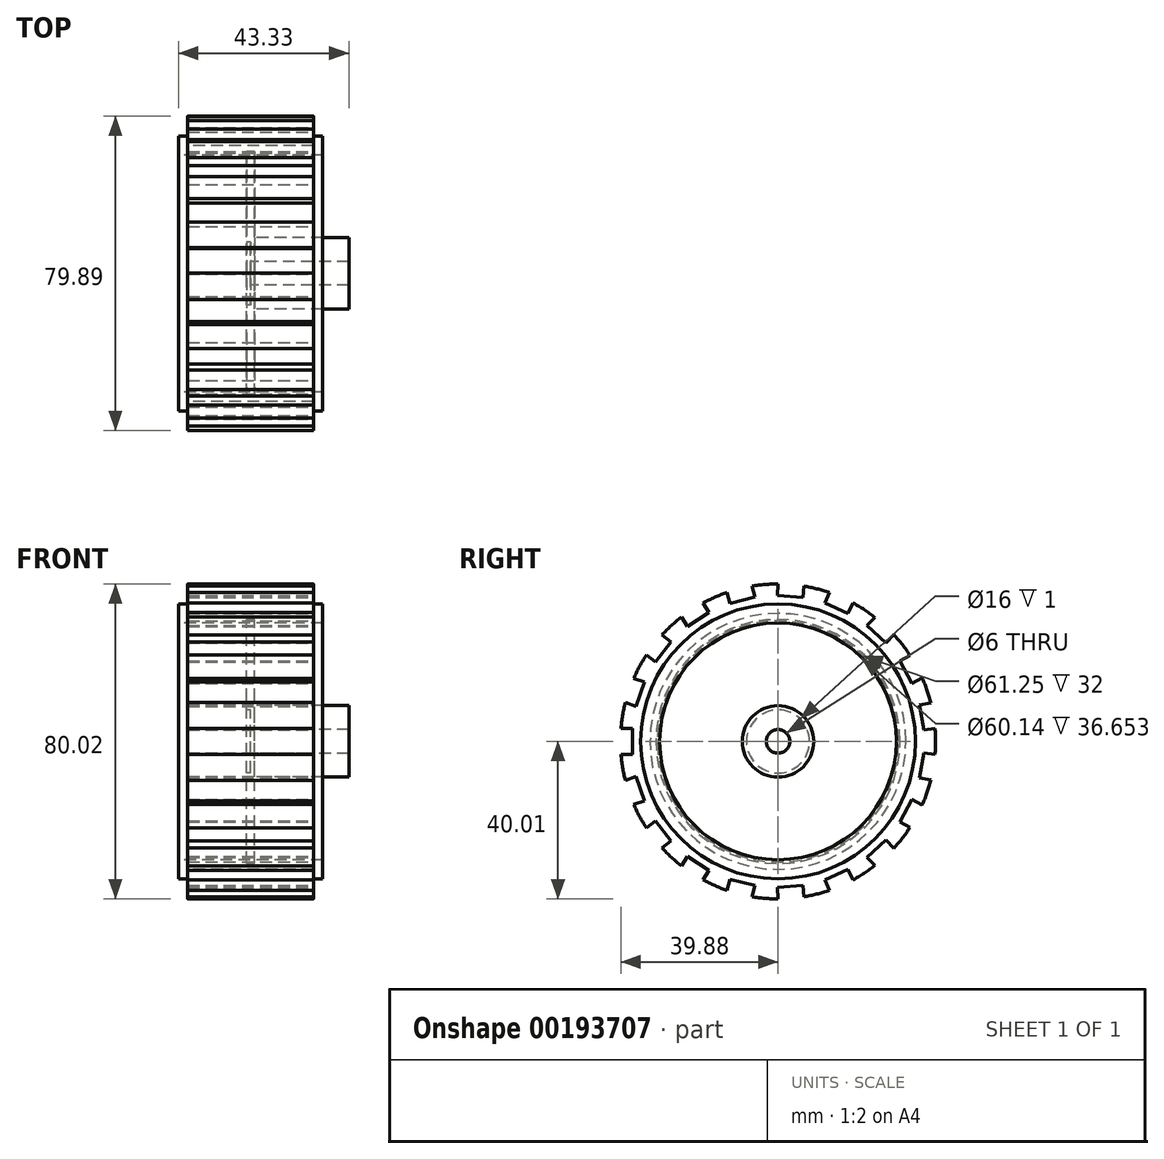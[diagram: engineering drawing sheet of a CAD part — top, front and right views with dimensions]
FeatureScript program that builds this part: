
annotation { "Feature Type Name" : "Feature", "Feature Type Description" : "" }
export const myFeature = defineFeature(function(context is Context, id is Id, definition is map)
    precondition{}
    {
        {
            var Q0;
            Q0=qCreatedBy(makeId("Front.planeOp"),FACE);
            var sketch = newSketch(context, id + "F0", { "sketchPlane" : qUnion([Q0])});
            skLineSegment(sketch, "E0.0", {"start": v(0, 32.5) * mm, "end": v(16, 32.5) * mm});
            skLineSegment(sketch, "E1", {"start": v(16, 32.5) * mm, "end": v(16, 34.92) * mm});
            skLineSegment(sketch, "E2", {"start": v(16, 34.92) * mm, "end": v(18.33, 34.92) * mm});
            skLineSegment(sketch, "E3", {"start": v(18.33, 34.92) * mm, "end": v(18.33, 30.07) * mm});
            skLineSegment(sketch, "E4", {"start": v(18.33, 30.07) * mm, "end": v(0, 30.07) * mm});
            skLineSegment(sketch, "E5.MirrorCS", {"start": v(-16, 32.5) * mm, "end": v(-16, 34.92) * mm});
            skLineSegment(sketch, "E6.MirrorCS", {"start": v(-16, 34.92) * mm, "end": v(-18.33, 34.92) * mm});
            skLineSegment(sketch, "E7.MirrorCS", {"start": v(0, 32.5) * mm, "end": v(-16, 32.5) * mm});
            skLineSegment(sketch, "E8.MirrorCS", {"start": v(-18.33, 34.92) * mm, "end": v(-18.33, 30.07) * mm});
            skLineSegment(sketch, "E9.MirrorCS", {"start": v(-18.33, 30.07) * mm, "end": v(0, 30.07) * mm});
            skLineSegment(sketch, "E10", {"start": v(-8.59, 0) * mm, "end": v(10.8, 0) * mm});
            skSolve(sketch);
        }
        {
            var Q0;
            Q0=makeQuery(id+"F0.imprint","IMPRINT",FACE,{"disambiguationData":[TD([[makeQuery(id+"F0.imprint","IMPRINT",EDGE,{"derivedFrom":sQuery(id+"F0.wireOp",EDGE,"E0.0")}),-1.0]])]});
            var Q1;
            Q1=sQuery(id+"F0.wireOp",EDGE,"E10");
            revolve(context, id + "F1", {"entities" : qUnion([Q0]), "axis" : qUnion([Q1]), "revolveType" : RevolveType.FULL});
        }
        {
            var Q0;
            Q0=qCreatedBy(makeId("Right.planeOp"),FACE);
            var sketch = newSketch(context, id + "F2", { "sketchPlane" : qUnion([Q0])});
            skCircle(sketch, "E11", {"center": v(0, 0) * mm, "radius": 31 * mm});
            skCircle(sketch, "E12", {"center": v(0, 0) * mm, "radius": 8 * mm});
            skCircle(sketch, "E13", {"center": v(0, 0) * mm, "radius": 3 * mm});
            skSolve(sketch);
        }
        {
            var Q0;
            Q0=makeQuery(id+"F2.imprint","IMPRINT",FACE,{"disambiguationData":[TD([[makeQuery(id+"F2.imprint","IMPRINT",EDGE,{"derivedFrom":sQuery(id+"F2.wireOp",EDGE,"E11")}),1.0]])]});
            extrude(context, id + "F3", {"entities" : qUnion([Q0]), "depth" : 1 * mm, "hasSecondDirection" : true, "secondDirectionOppositeDirection" : true, "secondDirectionDepth" : 1 * mm});
        }
        {
            var Q0;
            Q0=qCreatedBy(makeId("Right.planeOp"),FACE);
            var sketch = newSketch(context, id + "F4", { "sketchPlane" : qUnion([Q0])});
            skCircle(sketch, "E14", {"center": v(0, 0) * mm, "radius": 9.08 * mm});
            skCircle(sketch, "E15", {"center": v(0, 0) * mm, "radius": 3 * mm});
            skSolve(sketch);
        }
        {
            var Q0;
            Q0=qSketchRegion(id+"F4",true);
            extrude(context, id + "F5", {"entities" : qUnion([Q0]), "operationType" : NewBodyOperationType.ADD, "depth" : 25 * mm});
        }
        {
            var Q0;
            Q0=qCreatedBy(makeId("Right.planeOp"),FACE);
            cPlane(context, id + "F6", {"entities" : qUnion([Q0]), "cplaneType" : CPlaneType.OFFSET, "offset" : 16 * mm, "width" : 150 * mm, "height" : 150 * mm});
        }
        {
            var Q0;
            Q0=qCreatedBy(id+"F6.planeOp",FACE);
            var sketch = newSketch(context, id + "F7", { "sketchPlane" : qUnion([Q0])});
            skCircle(sketch, "E16", {"center": v(0, 0) * mm, "radius": 30.63 * mm});
            skCircle(sketch, "E17", {"center": v(0, 0) * mm, "radius": 40.01 * mm});
            skSolve(sketch);
        }
        {
            var Q0;
            Q0=qSketchRegion(id+"F7",true);
            extrude(context, id + "F8", {"entities" : qUnion([Q0]), "oppositeDirection" : true, "depth" : 32 * mm});
        }
        {
            var Q0;
            Q0=qCreatedBy(id+"F6.planeOp",FACE);
            var sketch = newSketch(context, id + "F9", { "sketchPlane" : qUnion([Q0])});
            skLineSegment(sketch, "E18.bottom", {"start": v(-36.97, -3.26) * mm, "end": v(-46.27, -3.26) * mm});
            skLineSegment(sketch, "E18.top", {"start": v(-36.97, 3.26) * mm, "end": v(-46.27, 3.26) * mm});
            skLineSegment(sketch, "E18.left", {"start": v(-36.97, -3.26) * mm, "end": v(-36.97, 3.26) * mm});
            skLineSegment(sketch, "E18.right", {"start": v(-46.27, -3.26) * mm, "end": v(-46.27, 3.26) * mm});
            skPoint(sketch, "E18.middle", {"position": v(-41.62, 0) * mm});
            skPoint(sketch, "E19.1.0", {"position": v(-39.37, 13.52) * mm});
            skLineSegment(sketch, "E19.1.1", {"start": v(-36.03, 8.93) * mm, "end": v(-44.82, 11.95) * mm});
            skLineSegment(sketch, "E19.1.2", {"start": v(-33.91, 15.08) * mm, "end": v(-42.71, 18.1) * mm});
            skLineSegment(sketch, "E19.1.3", {"start": v(-36.03, 8.93) * mm, "end": v(-33.91, 15.08) * mm});
            skLineSegment(sketch, "E19.1.4", {"start": v(-44.82, 11.95) * mm, "end": v(-42.71, 18.1) * mm});
            skPoint(sketch, "E19.2.0", {"position": v(-32.85, 25.57) * mm});
            skLineSegment(sketch, "E19.2.1", {"start": v(-31.18, 20.14) * mm, "end": v(-38.52, 25.85) * mm});
            skLineSegment(sketch, "E19.2.2", {"start": v(-27.18, 25.28) * mm, "end": v(-34.52, 31) * mm});
            skLineSegment(sketch, "E19.2.3", {"start": v(-31.18, 20.14) * mm, "end": v(-27.18, 25.28) * mm});
            skLineSegment(sketch, "E19.2.4", {"start": v(-38.52, 25.85) * mm, "end": v(-34.52, 31) * mm});
            skPoint(sketch, "E19.3.0", {"position": v(-22.77, 34.85) * mm});
            skLineSegment(sketch, "E19.3.1", {"start": v(-22.95, 29.17) * mm, "end": v(-28.04, 36.96) * mm});
            skLineSegment(sketch, "E19.3.2", {"start": v(-17.5, 32.73) * mm, "end": v(-22.58, 40.52) * mm});
            skLineSegment(sketch, "E19.3.3", {"start": v(-22.95, 29.17) * mm, "end": v(-17.5, 32.73) * mm});
            skLineSegment(sketch, "E19.3.4", {"start": v(-28.04, 36.96) * mm, "end": v(-22.58, 40.52) * mm});
            skPoint(sketch, "E19.4.0", {"position": v(-10.22, 40.35) * mm});
            skLineSegment(sketch, "E19.4.1", {"start": v(-12.23, 35.04) * mm, "end": v(-14.52, 44.06) * mm});
            skLineSegment(sketch, "E19.4.2", {"start": v(-5.92, 36.64) * mm, "end": v(-8.2, 45.66) * mm});
            skLineSegment(sketch, "E19.4.3", {"start": v(-12.23, 35.04) * mm, "end": v(-5.92, 36.64) * mm});
            skLineSegment(sketch, "E19.4.4", {"start": v(-14.52, 44.06) * mm, "end": v(-8.2, 45.66) * mm});
            skPoint(sketch, "E19.5.0", {"position": v(3.44, 41.48) * mm});
            skLineSegment(sketch, "E19.5.1", {"start": v(-0.2, 37.12) * mm, "end": v(0.58, 46.39) * mm});
            skLineSegment(sketch, "E19.5.2", {"start": v(6.3, 36.58) * mm, "end": v(7.07, 45.85) * mm});
            skLineSegment(sketch, "E19.5.3", {"start": v(-0.2, 37.12) * mm, "end": v(6.3, 36.58) * mm});
            skLineSegment(sketch, "E19.5.4", {"start": v(0.58, 46.39) * mm, "end": v(7.07, 45.85) * mm});
            skPoint(sketch, "E19.6.0", {"position": v(16.72, 38.12) * mm});
            skLineSegment(sketch, "E19.6.1", {"start": v(11.87, 35.17) * mm, "end": v(15.6, 43.68) * mm});
            skLineSegment(sketch, "E19.6.2", {"start": v(17.83, 32.55) * mm, "end": v(21.57, 41.07) * mm});
            skLineSegment(sketch, "E19.6.3", {"start": v(11.87, 35.17) * mm, "end": v(17.83, 32.55) * mm});
            skLineSegment(sketch, "E19.6.4", {"start": v(15.6, 43.68) * mm, "end": v(21.57, 41.07) * mm});
            skPoint(sketch, "E19.7.0", {"position": v(28.2, 30.62) * mm});
            skLineSegment(sketch, "E19.7.1", {"start": v(22.65, 29.4) * mm, "end": v(28.95, 36.25) * mm});
            skLineSegment(sketch, "E19.7.2", {"start": v(27.44, 25) * mm, "end": v(33.74, 31.84) * mm});
            skLineSegment(sketch, "E19.7.3", {"start": v(22.65, 29.4) * mm, "end": v(27.44, 25) * mm});
            skLineSegment(sketch, "E19.7.4", {"start": v(28.95, 36.25) * mm, "end": v(33.74, 31.84) * mm});
            skPoint(sketch, "E19.8.0", {"position": v(36.6, 19.81) * mm});
            skLineSegment(sketch, "E19.8.1", {"start": v(30.97, 20.46) * mm, "end": v(39.15, 24.89) * mm});
            skLineSegment(sketch, "E19.8.2", {"start": v(34.07, 14.73) * mm, "end": v(42.25, 19.16) * mm});
            skLineSegment(sketch, "E19.8.3", {"start": v(30.97, 20.46) * mm, "end": v(34.07, 14.73) * mm});
            skLineSegment(sketch, "E19.8.4", {"start": v(39.15, 24.89) * mm, "end": v(42.25, 19.16) * mm});
            skPoint(sketch, "E19.9.0", {"position": v(41.06, 6.85) * mm});
            skLineSegment(sketch, "E19.9.1", {"start": v(35.93, 9.3) * mm, "end": v(45.1, 10.83) * mm});
            skLineSegment(sketch, "E19.9.2", {"start": v(37, 2.87) * mm, "end": v(46.18, 4.4) * mm});
            skLineSegment(sketch, "E19.9.3", {"start": v(35.93, 9.3) * mm, "end": v(37, 2.87) * mm});
            skLineSegment(sketch, "E19.9.4", {"start": v(45.1, 10.83) * mm, "end": v(46.18, 4.4) * mm});
            skPoint(sketch, "E19.10.0", {"position": v(41.06, -6.85) * mm});
            skLineSegment(sketch, "E19.10.1", {"start": v(37, -2.87) * mm, "end": v(46.18, -4.4) * mm});
            skLineSegment(sketch, "E19.10.2", {"start": v(35.93, -9.3) * mm, "end": v(45.1, -10.83) * mm});
            skLineSegment(sketch, "E19.10.3", {"start": v(37, -2.87) * mm, "end": v(35.93, -9.3) * mm});
            skLineSegment(sketch, "E19.10.4", {"start": v(46.18, -4.4) * mm, "end": v(45.1, -10.83) * mm});
            skPoint(sketch, "E19.11.0", {"position": v(36.6, -19.81) * mm});
            skLineSegment(sketch, "E19.11.1", {"start": v(34.07, -14.73) * mm, "end": v(42.25, -19.16) * mm});
            skLineSegment(sketch, "E19.11.2", {"start": v(30.97, -20.46) * mm, "end": v(39.15, -24.89) * mm});
            skLineSegment(sketch, "E19.11.3", {"start": v(34.07, -14.73) * mm, "end": v(30.97, -20.46) * mm});
            skLineSegment(sketch, "E19.11.4", {"start": v(42.25, -19.16) * mm, "end": v(39.15, -24.89) * mm});
            skPoint(sketch, "E19.12.0", {"position": v(28.2, -30.62) * mm});
            skLineSegment(sketch, "E19.12.1", {"start": v(27.44, -25) * mm, "end": v(33.74, -31.84) * mm});
            skLineSegment(sketch, "E19.12.2", {"start": v(22.65, -29.4) * mm, "end": v(28.95, -36.25) * mm});
            skLineSegment(sketch, "E19.12.3", {"start": v(27.44, -25) * mm, "end": v(22.65, -29.4) * mm});
            skLineSegment(sketch, "E19.12.4", {"start": v(33.74, -31.84) * mm, "end": v(28.95, -36.25) * mm});
            skPoint(sketch, "E19.13.0", {"position": v(16.72, -38.12) * mm});
            skLineSegment(sketch, "E19.13.1", {"start": v(17.83, -32.55) * mm, "end": v(21.57, -41.07) * mm});
            skLineSegment(sketch, "E19.13.2", {"start": v(11.87, -35.17) * mm, "end": v(15.6, -43.68) * mm});
            skLineSegment(sketch, "E19.13.3", {"start": v(17.83, -32.55) * mm, "end": v(11.87, -35.17) * mm});
            skLineSegment(sketch, "E19.13.4", {"start": v(21.57, -41.07) * mm, "end": v(15.6, -43.68) * mm});
            skPoint(sketch, "E19.14.0", {"position": v(3.44, -41.48) * mm});
            skLineSegment(sketch, "E19.14.1", {"start": v(6.3, -36.58) * mm, "end": v(7.07, -45.85) * mm});
            skLineSegment(sketch, "E19.14.2", {"start": v(-0.2, -37.12) * mm, "end": v(0.58, -46.39) * mm});
            skLineSegment(sketch, "E19.14.3", {"start": v(6.3, -36.58) * mm, "end": v(-0.2, -37.12) * mm});
            skLineSegment(sketch, "E19.14.4", {"start": v(7.07, -45.85) * mm, "end": v(0.58, -46.39) * mm});
            skPoint(sketch, "E19.15.0", {"position": v(-10.22, -40.35) * mm});
            skLineSegment(sketch, "E19.15.1", {"start": v(-5.92, -36.64) * mm, "end": v(-8.2, -45.66) * mm});
            skLineSegment(sketch, "E19.15.2", {"start": v(-12.23, -35.04) * mm, "end": v(-14.52, -44.06) * mm});
            skLineSegment(sketch, "E19.15.3", {"start": v(-5.92, -36.64) * mm, "end": v(-12.23, -35.04) * mm});
            skLineSegment(sketch, "E19.15.4", {"start": v(-8.2, -45.66) * mm, "end": v(-14.52, -44.06) * mm});
            skPoint(sketch, "E19.16.0", {"position": v(-22.77, -34.85) * mm});
            skLineSegment(sketch, "E19.16.1", {"start": v(-17.5, -32.73) * mm, "end": v(-22.58, -40.52) * mm});
            skLineSegment(sketch, "E19.16.2", {"start": v(-22.95, -29.17) * mm, "end": v(-28.04, -36.96) * mm});
            skLineSegment(sketch, "E19.16.3", {"start": v(-17.5, -32.73) * mm, "end": v(-22.95, -29.17) * mm});
            skLineSegment(sketch, "E19.16.4", {"start": v(-22.58, -40.52) * mm, "end": v(-28.04, -36.96) * mm});
            skPoint(sketch, "E19.17.0", {"position": v(-32.85, -25.57) * mm});
            skLineSegment(sketch, "E19.17.1", {"start": v(-27.18, -25.28) * mm, "end": v(-34.52, -31) * mm});
            skLineSegment(sketch, "E19.17.2", {"start": v(-31.18, -20.14) * mm, "end": v(-38.52, -25.85) * mm});
            skLineSegment(sketch, "E19.17.3", {"start": v(-27.18, -25.28) * mm, "end": v(-31.18, -20.14) * mm});
            skLineSegment(sketch, "E19.17.4", {"start": v(-34.52, -31) * mm, "end": v(-38.52, -25.85) * mm});
            skPoint(sketch, "E19.18.0", {"position": v(-39.37, -13.52) * mm});
            skLineSegment(sketch, "E19.18.1", {"start": v(-33.91, -15.08) * mm, "end": v(-42.71, -18.1) * mm});
            skLineSegment(sketch, "E19.18.2", {"start": v(-36.03, -8.93) * mm, "end": v(-44.82, -11.95) * mm});
            skLineSegment(sketch, "E19.18.3", {"start": v(-33.91, -15.08) * mm, "end": v(-36.03, -8.93) * mm});
            skLineSegment(sketch, "E19.18.4", {"start": v(-42.71, -18.1) * mm, "end": v(-44.82, -11.95) * mm});
            skPoint(sketch, "E19.center", {"position": v(0, 0) * mm});
            skLineSegment(sketch, "E19.anchor1", {"start": v(0, 0) * mm, "end": v(-46.27, -3.26) * mm, "construction": true});
            skLineSegment(sketch, "E19.anchor2", {"start": v(0, 0) * mm, "end": v(-46.27, -3.26) * mm, "construction": true});
            skSolve(sketch);
        }
        {
            var Q0;
            Q0=qSketchRegion(id+"F9",true);
            extrude(context, id + "F10", {"entities" : qUnion([Q0]), "operationType" : NewBodyOperationType.REMOVE, "oppositeDirection" : true, "depth" : 88 * mm});
        }
    });
